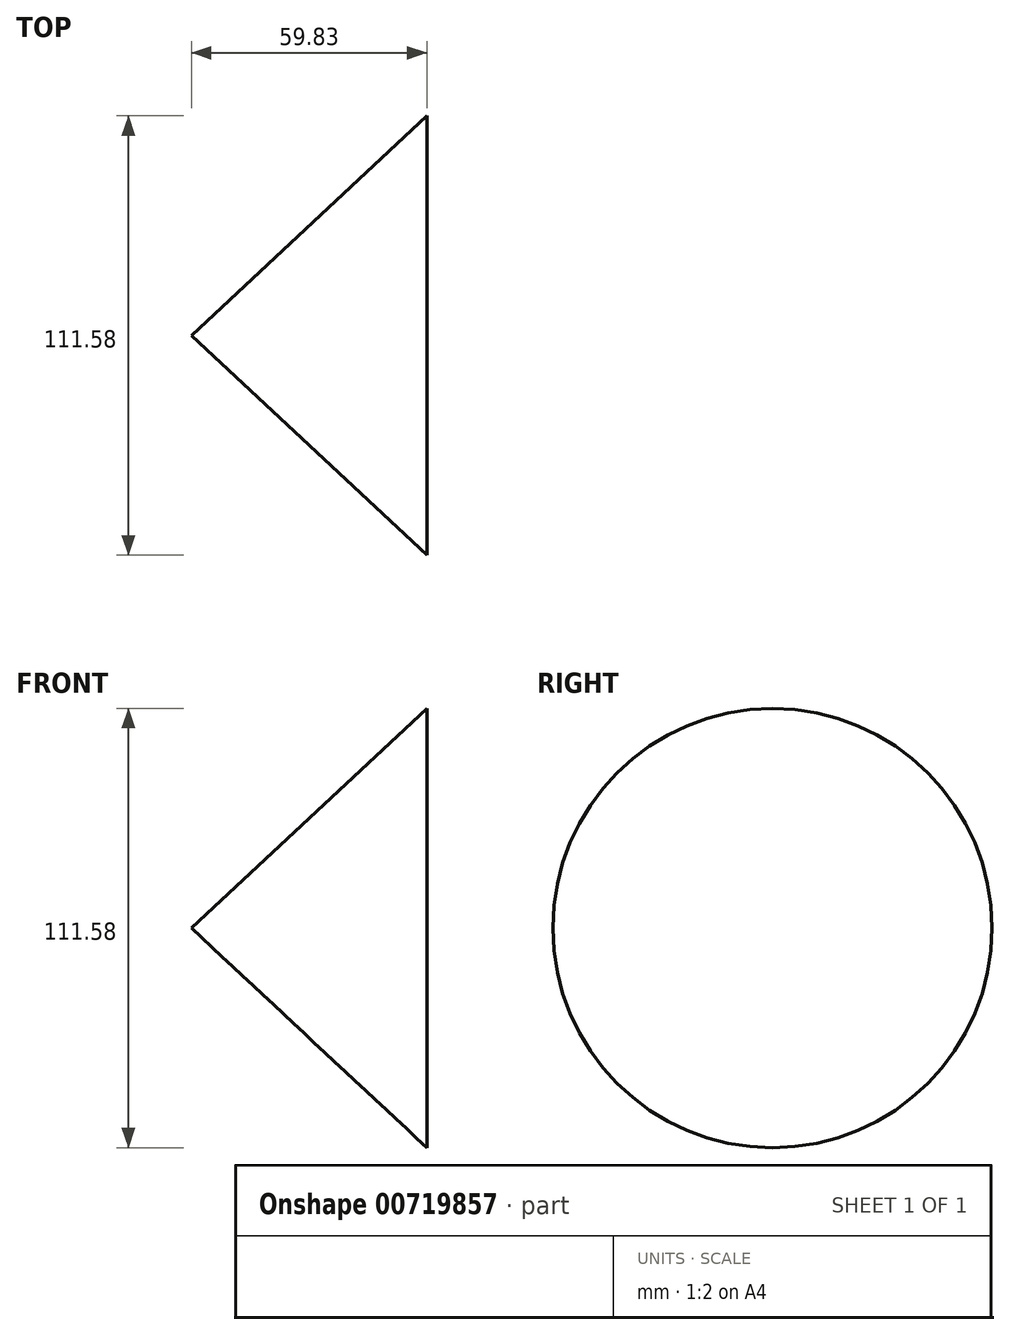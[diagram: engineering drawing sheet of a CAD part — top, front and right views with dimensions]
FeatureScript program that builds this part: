
annotation { "Feature Type Name" : "Feature", "Feature Type Description" : "" }
export const myFeature = defineFeature(function(context is Context, id is Id, definition is map)
    precondition{}
    {
        {
            var Q0;
            Q0=qCreatedBy(makeId("Front.planeOp"),FACE);
            var sketch = newSketch(context, id + "F0", { "sketchPlane" : qUnion([Q0])});
            skLineSegment(sketch, "E0", {"start": v(0, 55.8) * mm, "end": v(-59.83, 0) * mm});
            skLineSegment(sketch, "E1", {"start": v(-59.83, 0) * mm, "end": v(0, 0) * mm});
            skSolve(sketch);
        }
        {
            var Q0;
            Q0=sQuery(id+"F0.wireOp",EDGE,"E0");
            var Q1;
            Q1=sQuery(id+"F0.wireOp",EDGE,"E1");
            revolve(context, id + "F1", {"bodyType" : ToolBodyType.SURFACE, "surfaceOperationType" : NewSurfaceOperationType.NEW, "surfaceEntities" : qUnion([Q0]), "axis" : qUnion([Q1]), "revolveType" : RevolveType.FULL});
        }
    });
